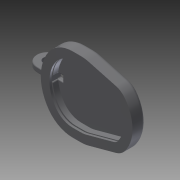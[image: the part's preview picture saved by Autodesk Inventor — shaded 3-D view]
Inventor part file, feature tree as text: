
AUTODESK INVENTOR PART (.ipt)
format: ipt  version: 2015 (Build 190159000, 159)  size: 638,976 bytes
history: native  units: mm
features: extrude x10, sketch x9, fillet x8, projected_geometry x6, plane x1
ambient origin geometry x8: Origin, YZ Plane, XZ Plane, XY Plane, X Axis, Y Axis, Z Axis, Center Point
bodies: Solid1 (feature_tree)
feature tree (34):
  extrude  "Extrusion1"  Depth=70.0mm
  fillet  "Fillet1"  Radius=5.0mm
  extrude  "Extrusion2"  Depth=12.0mm TaperAngle=0.0deg
  fillet  "Fillet6"  Radius=15.0mm
  fillet  "Fillet7"  Radius=85.0mm
  extrude  "Extrusion6"  Depth=45.0mm
  extrude  "Extrusion7"  [1 undecoded]
  plane  "Work Plane2"
  extrude  "Extrusion8"  Depth=3.0mm
  fillet  "Fillet8"  Radius=8.0mm
  fillet  "Fillet9"  Radius=20.0mm
  extrude  "Extrusion9"  Depth=15.5mm TaperAngle=0.0deg
  extrude  "Extrusion10"  Depth=1.0mm
  fillet  "Fillet10"  Radius=4.0mm
  extrude  "Extrusion12"  Depth=4.0mm
  extrude  "Extrusion13"  Depth=1.0mm
  fillet  "Fillet16"  Radius=2.0mm
  fillet  "Fillet19"  Radius=3.0mm
  extrude  "Extrusion14"  Depth=2.0mm TaperAngle=0.0deg
  sketch  "Sketch1"  dims[d0=80.0mm d1=70.0mm d2=5.0mm]
  sketch  "Sketch2"  dims[d3=5.0mm d4=12.0mm d5=0.0mm d6=15.0mm d9=85.0mm]
  sketch  "Sketch6"  dims[d12=48.333333mm d13=45.0mm]
  projected_geometry  "Projected Loop3"
  sketch  "Sketch9"  dims[d14=69.25mm d15=0.0mm d33=-1.666667mm]
  projected_geometry  "Projected Loop4"
  sketch  "Sketch10"  dims[d34=27.0mm d35=3.0mm d37=8.0mm d38=0.0mm d41=20.0mm]
  projected_geometry  "Projected Loop5"
  sketch  "Sketch11"  dims[d43=5.0mm d44=0.0mm d49=15.5mm d50=0.0mm]
  sketch  "Sketch13"  dims[d51=4.0mm d52=1.0mm d53=4.0mm]
  projected_geometry  "Projected Loop8"
  sketch  "Sketch16"  dims[d54=1.0mm d55=4.0mm]
  projected_geometry  "Projected Loop9"
  sketch  "Sketch17"  dims[d56=4.0mm d57=1.0mm d58=2.0mm d60=3.0mm d61=0.0mm d63=2.0mm d64=0.0mm d65=20.0mm d66=4.0mm d71=3.0mm d72=0.0mm d77=9.25mm d78=0.0mm d83=4.0mm d85=8.0mm d86=5.0mm d87=5.0mm d90=8.0mm d92=3.0mm d94=3.0mm d95=1.666667mm d96=1.0mm d99=261.0mm d100=2.0mm d101=0.0mm]
  projected_geometry  "Projected Loop10"
note: 1 required parameter value undecoded (feature->parameter linkage not recoverable at this tier; creation-order binding heuristic only, values carry confidence <= 0.55)
